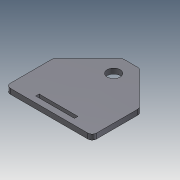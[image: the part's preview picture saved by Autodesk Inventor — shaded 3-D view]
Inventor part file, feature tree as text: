
AUTODESK INVENTOR PART (.ipt)
format: ipt  version: 2015 (Build 190159000, 159)  size: 129,024 bytes
history: native  units: mm
features: sketch x2, other x2, sheet_metal_op x1, hole x1, chamfer x1, plane x1
ambient origin geometry x8: Origin, YZ Plane, XZ Plane, XY Plane, X Axis, Y Axis, Z Axis, Center Point
bodies: Solid1 (feature_tree)
feature tree (8):
  sheet_metal_op  "Face1"
  hole  "Hole1"  [1 undecoded]
  chamfer  "Corner Round1"
  plane  "Work Plane1"
  sketch  "Sketch1"  dims[d2=95.0mm d3=100.0mm]
  other  "Plate1"
  sketch  "Sketch2"  dims[d4=40.0mm d5=40.0mm d6=40.0mm d7=40.0mm d8=0.001mm d9=20.0mm d10=50.0mm d11=15.0mm d12=6.0mm d13=4.0mm d14=2.0mm d15=90.0deg d16=6.0mm d17=20.594885mm d18=5.0mm d19=4.0mm d20=45.0mm d21=7.0mm d22=22.5mm d23=6.0mm d24=0.0mm]
  other  "Cut1"
note: 1 required parameter value undecoded (feature->parameter linkage not recoverable at this tier; creation-order binding heuristic only, values carry confidence <= 0.55)
